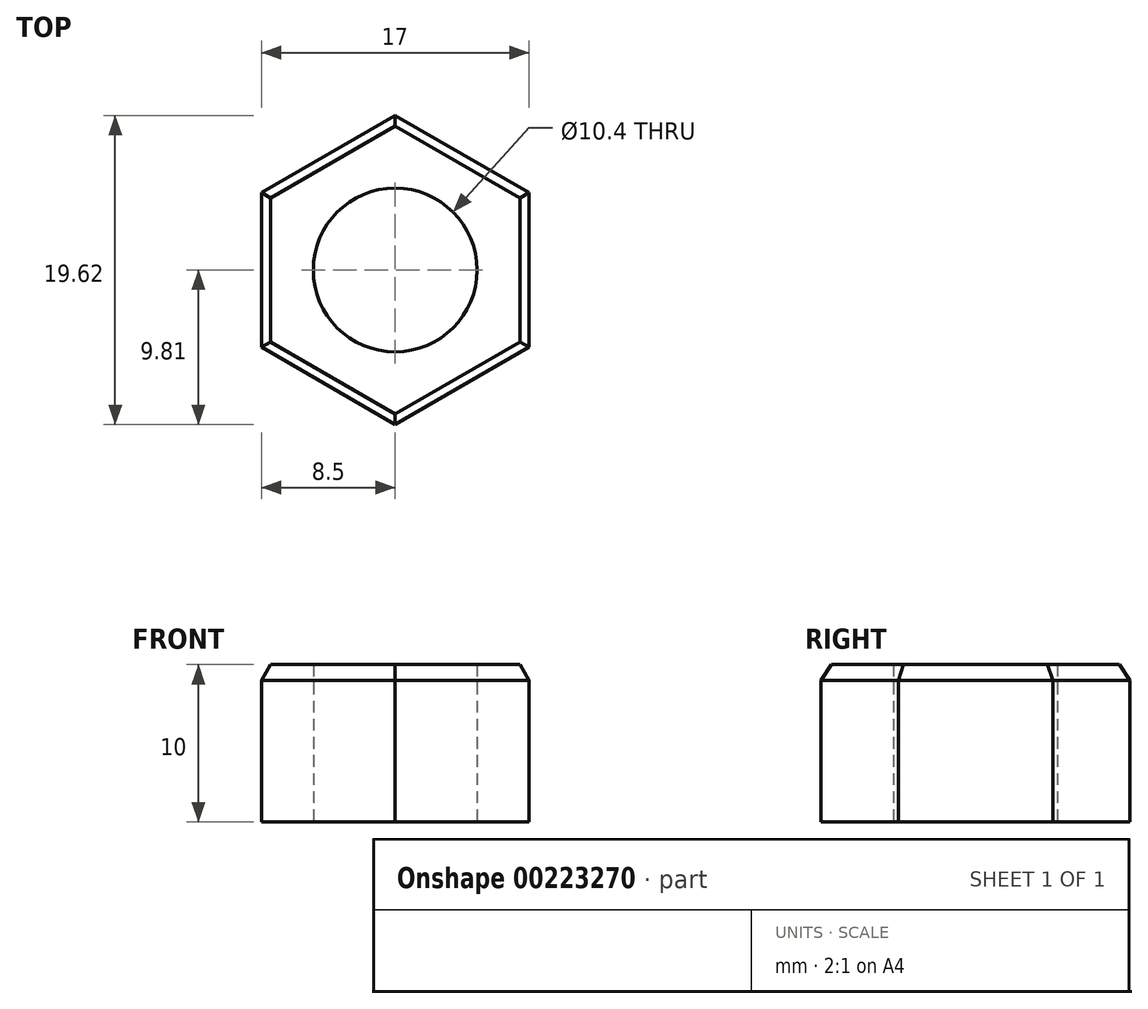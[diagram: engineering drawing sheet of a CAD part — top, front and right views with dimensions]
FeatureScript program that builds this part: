
annotation { "Feature Type Name" : "Feature", "Feature Type Description" : "" }
export const myFeature = defineFeature(function(context is Context, id is Id, definition is map)
    precondition{}
    {
        {
            var Q0;
            Q0=qCreatedBy(makeId("Top.planeOp"),FACE);
            var sketch = newSketch(context, id + "F0", { "sketchPlane" : qUnion([Q0])});
            skCircle(sketch, "E0.cCircle", {"center": v(0, 0) * mm, "radius": 8.5 * mm, "construction": true});
            skLineSegment(sketch, "E0.0", {"start": v(8.5, 4.9) * mm, "end": v(8.5, -4.9) * mm});
            skLineSegment(sketch, "E0.1", {"start": v(8.5, -4.9) * mm, "end": v(0, -9.81) * mm});
            skLineSegment(sketch, "E0.2", {"start": v(0, -9.81) * mm, "end": v(-8.5, -4.9) * mm});
            skLineSegment(sketch, "E0.3", {"start": v(-8.5, -4.9) * mm, "end": v(-8.5, 4.9) * mm});
            skLineSegment(sketch, "E0.4", {"start": v(-8.5, 4.9) * mm, "end": v(0, 9.81) * mm});
            skLineSegment(sketch, "E0.5", {"start": v(0, 9.81) * mm, "end": v(8.5, 4.9) * mm});
            skPoint(sketch, "E0.0.midPoint", {"position": v(8.5, 0) * mm});
            skCircle(sketch, "E1", {"center": v(0, 0) * mm, "radius": 5.2 * mm});
            skSolve(sketch);
        }
        {
            var Q0;
            Q0 = qSketchRegion(id + "F0", true);
            extrude(context, id + "F1", {"entities" : qUnion([Q0]), "depth" : 10 * mm});
        }
        {
            var Q0;
            Q0=makeQuery(id+"F1.opExtrude","CAP_EDGE",EDGE,{"disambiguationData":[OSD([sQuery(id+"F0.wireOp",EDGE,"E0.4")])],"isStart":false});
            var Q1;
            Q1=makeQuery(id+"F1.opExtrude","CAP_EDGE",EDGE,{"disambiguationData":[OSD([sQuery(id+"F0.wireOp",EDGE,"E0.5")])],"isStart":false});
            var Q2;
            Q2=makeQuery(id+"F1.opExtrude","CAP_EDGE",EDGE,{"disambiguationData":[OSD([sQuery(id+"F0.wireOp",EDGE,"E0.0")])],"isStart":false});
            var Q3;
            Q3=makeQuery(id+"F1.opExtrude","CAP_EDGE",EDGE,{"disambiguationData":[OSD([sQuery(id+"F0.wireOp",EDGE,"E0.1")])],"isStart":false});
            var Q4;
            Q4=makeQuery(id+"F1.opExtrude","CAP_EDGE",EDGE,{"disambiguationData":[OSD([sQuery(id+"F0.wireOp",EDGE,"E0.2")])],"isStart":false});
            var Q5;
            Q5=makeQuery(id+"F1.opExtrude","CAP_EDGE",EDGE,{"disambiguationData":[OSD([sQuery(id+"F0.wireOp",EDGE,"E0.3")])],"isStart":false});
            chamfer(context, id + "F2", {"entities" : qUnion([Q0, Q1, Q2, Q3, Q4, Q5]), "chamferType" : ChamferType.OFFSET_ANGLE, "width" : 1 * mm, "oppositeDirection" : false, "angle" : 30 * degree, "tangentPropagation" : true});
        }
    });
